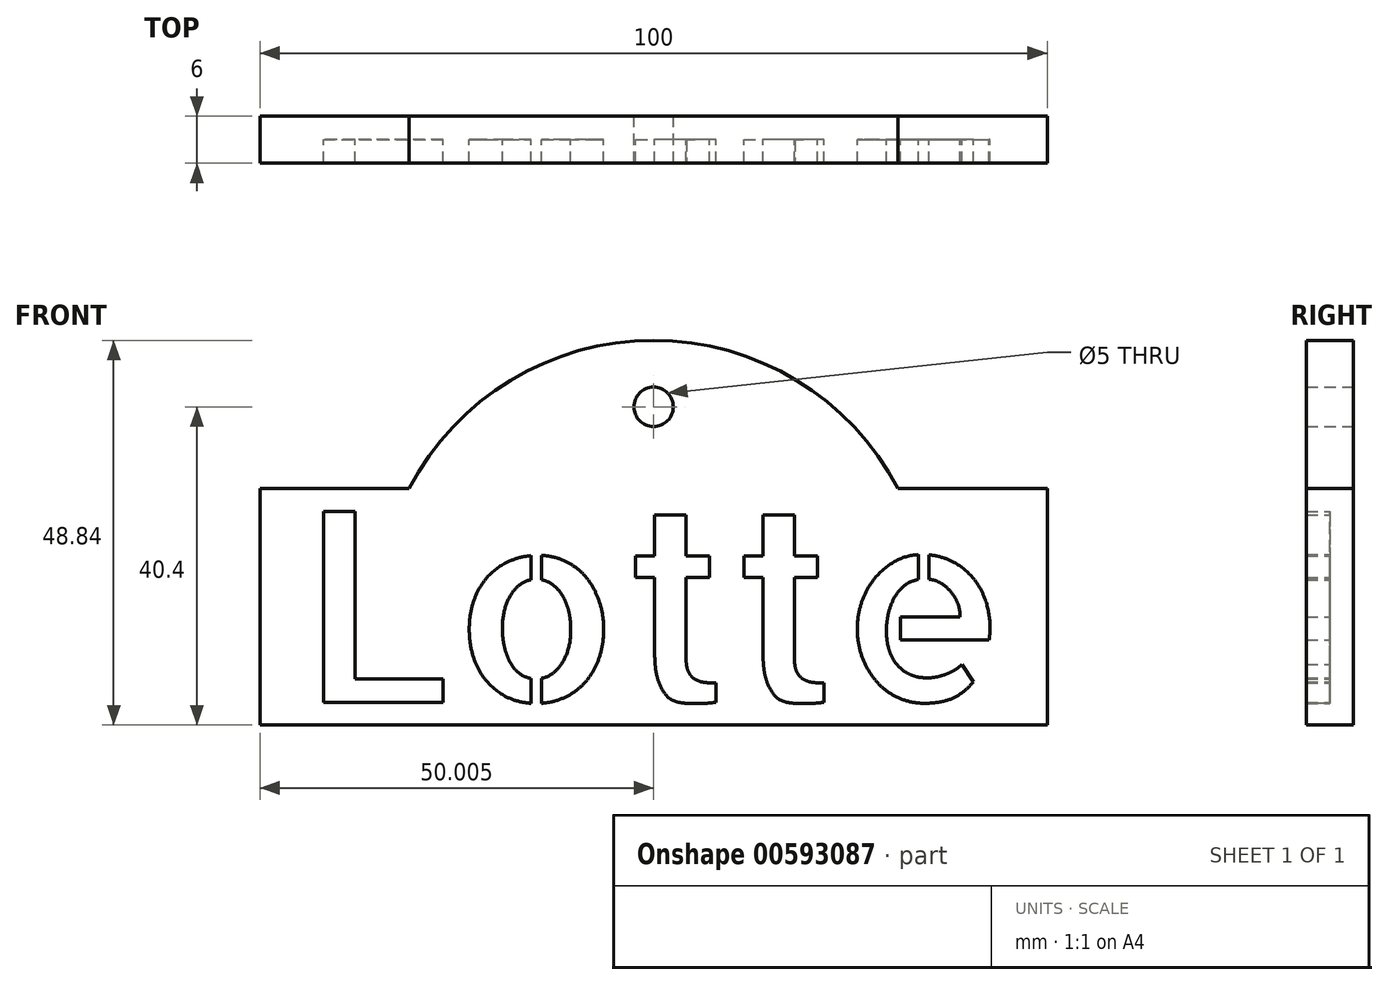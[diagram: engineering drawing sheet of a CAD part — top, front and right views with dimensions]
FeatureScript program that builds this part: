
annotation { "Feature Type Name" : "Feature", "Feature Type Description" : "" }
export const myFeature = defineFeature(function(context is Context, id is Id, definition is map)
    precondition{}
    {
        {
            var Q0;
            Q0=qCreatedBy(makeId("Front.planeOp"),FACE);
            var sketch = newSketch(context, id + "F0", { "sketchPlane" : qUnion([Q0])});
            skLineSegment(sketch, "E0.bottom", {"start": v(-67.68, 49.4) * mm, "end": v(-48.72, 49.4) * mm});
            skLineSegment(sketch, "E0.top", {"start": v(-67.68, 19.4) * mm, "end": v(32.32, 19.4) * mm});
            skLineSegment(sketch, "E0.left", {"start": v(-67.68, 49.4) * mm, "end": v(-67.68, 19.4) * mm});
            skLineSegment(sketch, "E0.right", {"start": v(32.32, 49.4) * mm, "end": v(32.32, 19.4) * mm});
            skArc(sketch, "E1", {"start": v(13.37, 49.4) * mm, "mid": v(-17.68, 68.23) * mm, "end": v(-48.72, 49.4) * mm});
            skCircle(sketch, "E2", {"center": v(-17.68, 59.8) * mm, "radius": 2.5 * mm});
            skText(sketch, "E3", { "text": "Lotte", "fontName": "AllertaStencil-Regular.ttf"});
            skPoint(sketch, "E4", {"position": v(-17.68, 19.4) * mm});
            skPoint(sketch, "E5", {"position": v(-17.68, 68.23) * mm});
            skPoint(sketch, "E6", {"position": v(32.32, 34.4) * mm});
            skPoint(sketch, "E7", {"position": v(27.32, 34.4) * mm});
            skLineSegment(sketch, "E8.trimOffspring", {"start": v(13.37, 49.4) * mm, "end": v(32.32, 49.4) * mm});
            const initialGuessF0  = {"E3": [-0.06268, 0.02226, 1, 0, 0.02426]};
            skSetInitialGuess(sketch, initialGuessF0);
            skSolve(sketch);
        }
        {
            var Q0;
            Q0 = qSketchRegion(id + "F0", true);
            var Q1;
            Q1=makeQuery(id+"F0.imprint","IMPRINT",FACE,{"disambiguationData":[TD([[makeQuery(id+"F0.imprint","IMPRINT",EDGE,{"derivedFrom":sQuery(id+"F0.wireOp",EDGE,"E3.sketch_text.stroke-0")}),-1.0]])]});
            var Q2;
            Q2=makeQuery(id+"F0.imprint","IMPRINT",FACE,{"disambiguationData":[TD([[makeQuery(id+"F0.imprint","IMPRINT",EDGE,{"derivedFrom":sQuery(id+"F0.wireOp",EDGE,"E3.sketch_text.stroke-6")}),-1.0]])]});
            var Q3;
            Q3=makeQuery(id+"F0.imprint","IMPRINT",FACE,{"disambiguationData":[TD([[makeQuery(id+"F0.imprint","IMPRINT",EDGE,{"derivedFrom":sQuery(id+"F0.wireOp",EDGE,"E3.sketch_text.stroke-22")}),-1.0]])]});
            var Q4;
            Q4=makeQuery(id+"F0.imprint","IMPRINT",FACE,{"disambiguationData":[TD([[makeQuery(id+"F0.imprint","IMPRINT",EDGE,{"derivedFrom":sQuery(id+"F0.wireOp",EDGE,"E3.sketch_text.stroke-38")}),-1.0]])]});
            var Q5;
            Q5=makeQuery(id+"F0.imprint","IMPRINT",FACE,{"disambiguationData":[TD([[makeQuery(id+"F0.imprint","IMPRINT",EDGE,{"derivedFrom":sQuery(id+"F0.wireOp",EDGE,"E3.sketch_text.stroke-63")}),-1.0]])]});
            var Q6;
            Q6=makeQuery(id+"F0.imprint","IMPRINT",FACE,{"disambiguationData":[TD([[makeQuery(id+"F0.imprint","IMPRINT",EDGE,{"derivedFrom":sQuery(id+"F0.wireOp",EDGE,"E3.sketch_text.stroke-88")}),-1.0]])]});
            var Q7;
            Q7=makeQuery(id+"F0.imprint","IMPRINT",FACE,{"disambiguationData":[TD([[makeQuery(id+"F0.imprint","IMPRINT",EDGE,{"derivedFrom":sQuery(id+"F0.wireOp",EDGE,"E3.sketch_text.stroke-101")}),-1.0]])]});
            var Q8;
            Q8=makeQuery(id+"F0.imprint","IMPRINT",FACE,{"disambiguationData":[TD([[makeQuery(id+"F0.imprint","IMPRINT",EDGE,{"derivedFrom":sQuery(id+"F0.wireOp",EDGE,"E0.bottom")}),-1.0]])]});
            extrude(context, id + "F1", {"entities" : qUnion([Q0, Q1, Q2, Q3, Q4, Q5, Q6, Q7, Q8]), "depth" : 3 * mm, "offsetDistance" : 25 * mm});
        }
        {
            var Q0;
            Q0=makeQuery(id+"F0.imprint","IMPRINT",FACE,{"disambiguationData":[TD([[makeQuery(id+"F0.imprint","IMPRINT",EDGE,{"derivedFrom":sQuery(id+"F0.wireOp",EDGE,"E0.bottom")}),-1.0]])]});
            extrude(context, id + "F2", {"entities" : qUnion([Q0]), "operationType" : NewBodyOperationType.ADD, "depth" : 6 * mm, "offsetDistance" : 25 * mm});
        }
    });
